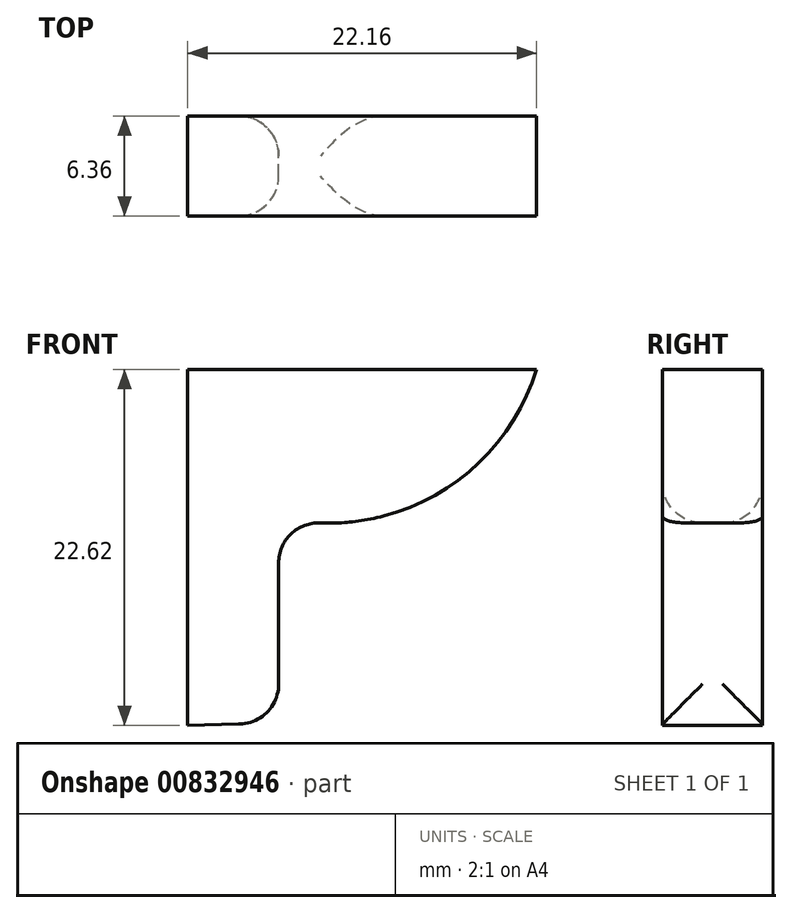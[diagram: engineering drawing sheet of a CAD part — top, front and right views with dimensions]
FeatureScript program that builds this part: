
annotation { "Feature Type Name" : "Feature", "Feature Type Description" : "" }
export const myFeature = defineFeature(function(context is Context, id is Id, definition is map)
    precondition{}
    {
        {
            var Q0;
            Q0=qCreatedBy(makeId("Front.planeOp"),FACE);
            var sketch = newSketch(context, id + "F0", { "sketchPlane" : qUnion([Q0])});
            skLineSegment(sketch, "E0.right", {"start": v(-3.03, 17.75) * mm, "end": v(-3.03, -4.7) * mm});
            skLineSegment(sketch, "E1", {"start": v(-3.03, 17.75) * mm, "end": v(13.34, 17.75) * mm});
            skArc(sketch, "E2", {"start": v(-3.03, 8.37) * mm, "mid": v(7, 9.82) * mm, "end": v(13.34, 17.75) * mm});
            skLineSegment(sketch, "E3", {"start": v(-3.03, 17.75) * mm, "end": v(-8.82, 17.75) * mm});
            skLineSegment(sketch, "E4", {"start": v(-8.82, 17.75) * mm, "end": v(-8.82, -4.87) * mm});
            skLineSegment(sketch, "E5", {"start": v(-8.82, -4.87) * mm, "end": v(-3.03, -4.7) * mm});
            skSolve(sketch);
        }
        {
            var Q0;
            Q0 = qSketchRegion(id + "F0", true);
            extrude(context, id + "F1", {"entities" : qUnion([Q0]), "endBound" : BoundingType.SYMMETRIC, "depth" : 6.35 * mm, "offsetDistance" : 25.4 * mm});
        }
        {
            var Q0;
            Q0=makeQuery(id+"F1.opExtrude","SWEPT_FACE",FACE,{"disambiguationData":[OSD([sQuery(id+"F0.wireOp",EDGE,"E0.right")])]});
            fillet(context, id + "F2", {"entities" : qUnion([Q0]), "radius" : 2.54 * mm, "tangentPropagation" : true, "allowEdgeOverflow" : false});
        }
    });
